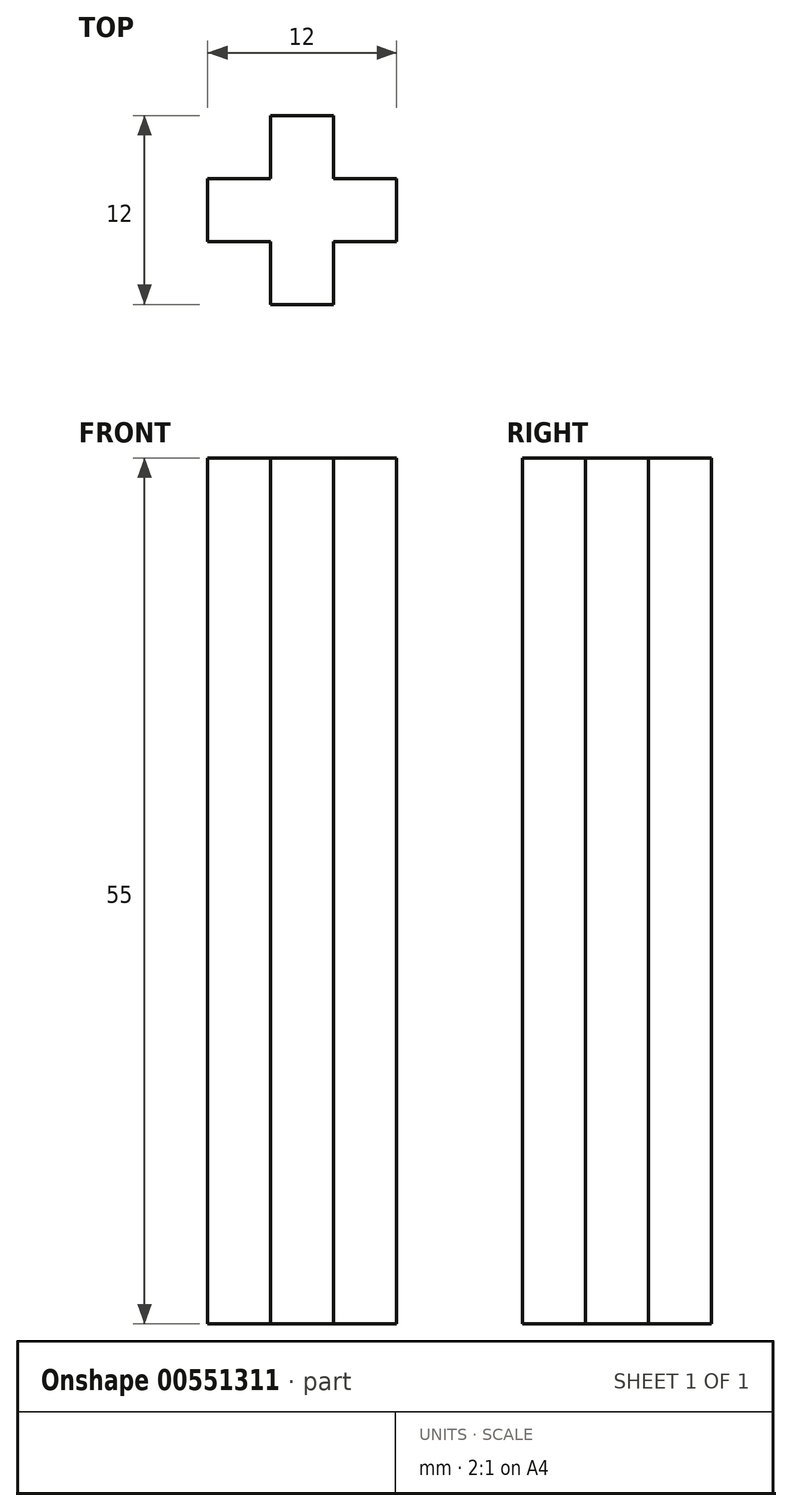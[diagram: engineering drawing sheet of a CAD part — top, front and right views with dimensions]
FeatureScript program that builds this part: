
annotation { "Feature Type Name" : "Feature", "Feature Type Description" : "" }
export const myFeature = defineFeature(function(context is Context, id is Id, definition is map)
    precondition{}
    {
        {
            var Q0;
            Q0=qCreatedBy(makeId("Top.planeOp"),FACE);
            var sketch = newSketch(context, id + "F0", { "sketchPlane" : qUnion([Q0])});
            skLineSegment(sketch, "E0", {"start": v(-1.19, 4.8) * mm, "end": v(2.81, 4.8) * mm});
            skLineSegment(sketch, "E1", {"start": v(2.81, 4.8) * mm, "end": v(2.81, 0.8) * mm});
            skLineSegment(sketch, "E2", {"start": v(2.81, 0.8) * mm, "end": v(6.81, 0.8) * mm});
            skLineSegment(sketch, "E3", {"start": v(6.81, 0.8) * mm, "end": v(6.81, -3.2) * mm});
            skLineSegment(sketch, "E4", {"start": v(6.81, -3.2) * mm, "end": v(2.81, -3.2) * mm});
            skLineSegment(sketch, "E5", {"start": v(2.81, -3.2) * mm, "end": v(2.81, -7.2) * mm});
            skLineSegment(sketch, "E6", {"start": v(2.81, -7.2) * mm, "end": v(-1.19, -7.2) * mm});
            skLineSegment(sketch, "E7", {"start": v(-1.19, -7.2) * mm, "end": v(-1.19, -3.2) * mm});
            skLineSegment(sketch, "E8", {"start": v(-1.19, -3.2) * mm, "end": v(-5.19, -3.2) * mm});
            skLineSegment(sketch, "E9", {"start": v(-5.19, -3.2) * mm, "end": v(-5.19, 0.8) * mm});
            skLineSegment(sketch, "E10", {"start": v(-5.19, 0.8) * mm, "end": v(-1.19, 0.8) * mm});
            skLineSegment(sketch, "E11", {"start": v(-1.19, 0.8) * mm, "end": v(-1.19, 4.8) * mm});
            skSolve(sketch);
        }
        {
            var Q0;
            Q0=makeQuery(id+"F0.imprint","IMPRINT",FACE,{"disambiguationData":[TD([[makeQuery(id+"F0.imprint","IMPRINT",EDGE,{"derivedFrom":sQuery(id+"F0.wireOp",EDGE,"E0")}),-1.0]])]});
            extrude(context, id + "F1", {"entities" : qUnion([Q0]), "depth" : 55 * mm, "offsetDistance" : 25.4 * mm});
        }
    });
